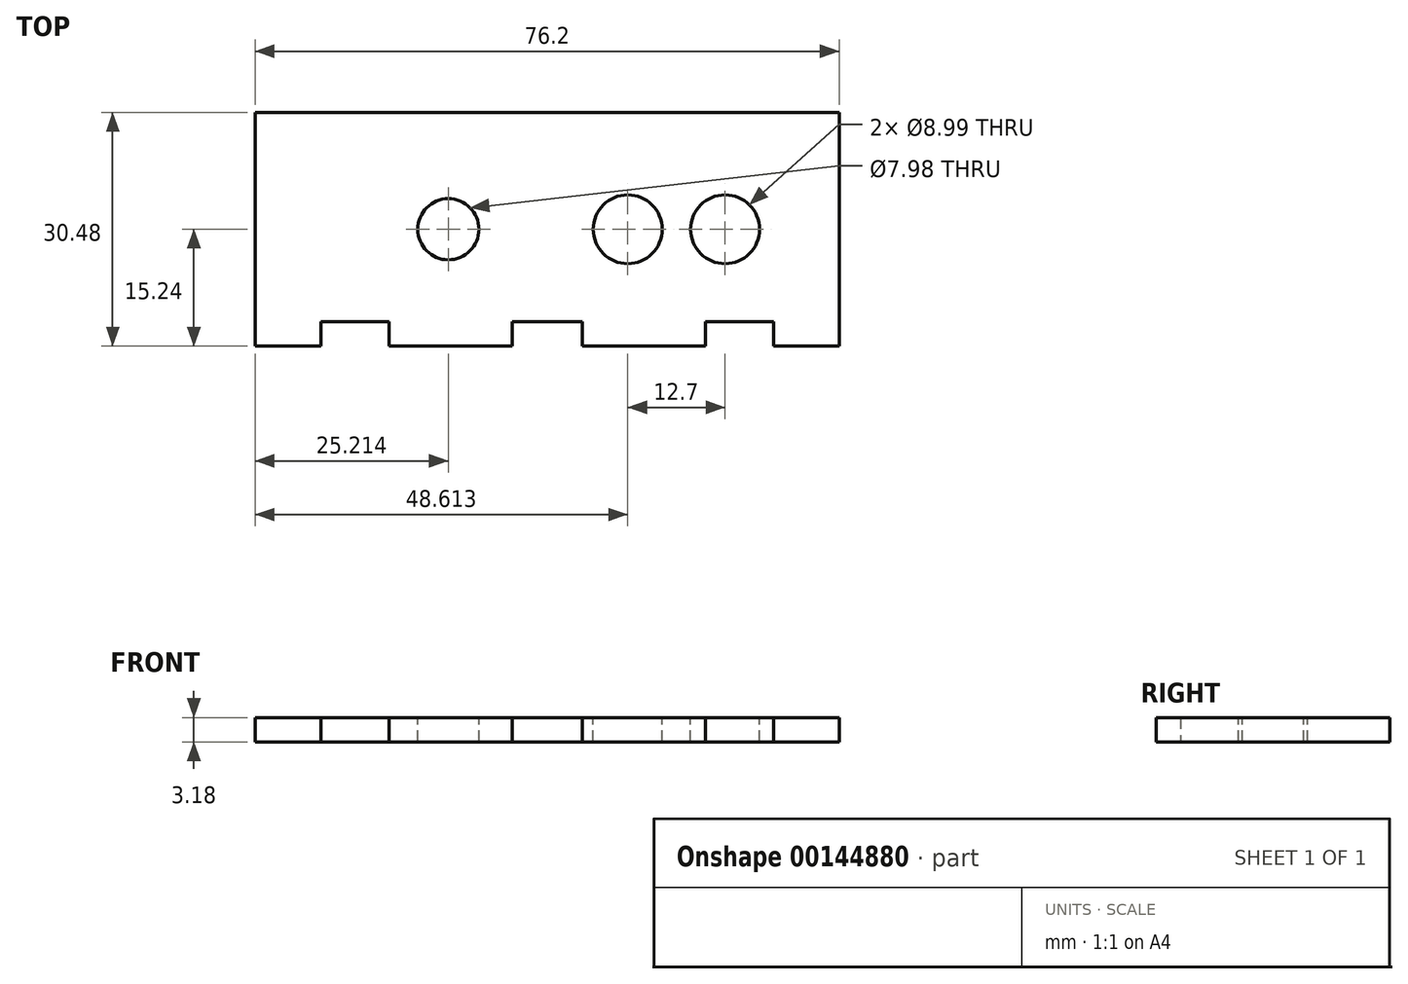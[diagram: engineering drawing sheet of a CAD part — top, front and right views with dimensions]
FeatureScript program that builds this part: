
annotation { "Feature Type Name" : "Feature", "Feature Type Description" : "" }
export const myFeature = defineFeature(function(context is Context, id is Id, definition is map)
    precondition{}
    {
        {
            var Q0;
            Q0=qCreatedBy(makeId("Top.planeOp"),FACE);
            var sketch = newSketch(context, id + "F0", { "sketchPlane" : qUnion([Q0])});
            skLineSegment(sketch, "E0.bottom", {"start": v(-38.1, 15.24) * mm, "end": v(38.1, 15.24) * mm});
            skLineSegment(sketch, "E0.top", {"start": v(-38.1, -15.24) * mm, "end": v(38.1, -15.24) * mm});
            skLineSegment(sketch, "E0.left", {"start": v(-38.1, 15.24) * mm, "end": v(-38.1, -15.24) * mm});
            skLineSegment(sketch, "E0.right", {"start": v(38.1, 15.24) * mm, "end": v(38.1, -15.24) * mm});
            skPoint(sketch, "E0.middle", {"position": v(0, 0) * mm});
            skLineSegment(sketch, "E1.bottom", {"start": v(-29.51, 15.24) * mm, "end": v(-20.62, 15.24) * mm});
            skLineSegment(sketch, "E2.bottom", {"start": v(29.51, 15.24) * mm, "end": v(20.62, 15.24) * mm});
            skLineSegment(sketch, "E3.top", {"start": v(-29.51, 18.42) * mm, "end": v(-20.62, 18.42) * mm});
            skLineSegment(sketch, "E3.left", {"start": v(-29.51, 15.24) * mm, "end": v(-29.51, 18.42) * mm});
            skLineSegment(sketch, "E3.right", {"start": v(-20.62, 15.24) * mm, "end": v(-20.62, 18.41) * mm});
            skLineSegment(sketch, "E4.top", {"start": v(20.62, 18.42) * mm, "end": v(29.51, 18.42) * mm});
            skLineSegment(sketch, "E4.left", {"start": v(20.62, 15.24) * mm, "end": v(20.62, 18.42) * mm});
            skLineSegment(sketch, "E4.right", {"start": v(29.51, 15.24) * mm, "end": v(29.51, 18.42) * mm});
            skPoint(sketch, "E5", {"position": v(0, 15.24) * mm});
            skPoint(sketch, "E6", {"position": v(-4.57, 15.24) * mm});
            skPoint(sketch, "E7", {"position": v(4.57, 15.24) * mm});
            skLineSegment(sketch, "E8.bottom", {"start": v(-4.57, 15.24) * mm, "end": v(4.57, 15.24) * mm});
            skLineSegment(sketch, "E8.top", {"start": v(-4.57, 18.42) * mm, "end": v(4.57, 18.42) * mm});
            skLineSegment(sketch, "E8.left", {"start": v(-4.57, 15.24) * mm, "end": v(-4.57, 18.42) * mm});
            skLineSegment(sketch, "E8.right", {"start": v(4.57, 15.24) * mm, "end": v(4.57, 18.42) * mm});
            skLineSegment(sketch, "E9.bottom", {"start": v(-29.51, -15.24) * mm, "end": v(-20.62, -15.24) * mm});
            skLineSegment(sketch, "E9.top", {"start": v(-29.51, -12.06) * mm, "end": v(-20.62, -12.06) * mm});
            skLineSegment(sketch, "E9.left", {"start": v(-29.51, -15.24) * mm, "end": v(-29.51, -12.06) * mm});
            skLineSegment(sketch, "E9.right", {"start": v(-20.62, -15.24) * mm, "end": v(-20.62, -12.06) * mm});
            skLineSegment(sketch, "E10.bottom", {"start": v(-4.57, -15.24) * mm, "end": v(4.57, -15.24) * mm});
            skLineSegment(sketch, "E10.top", {"start": v(-4.57, -12.06) * mm, "end": v(4.57, -12.06) * mm});
            skLineSegment(sketch, "E10.left", {"start": v(-4.57, -15.24) * mm, "end": v(-4.57, -12.06) * mm});
            skLineSegment(sketch, "E10.right", {"start": v(4.57, -15.24) * mm, "end": v(4.57, -12.06) * mm});
            skLineSegment(sketch, "E11.bottom", {"start": v(20.62, -15.24) * mm, "end": v(29.51, -15.24) * mm});
            skLineSegment(sketch, "E11.top", {"start": v(20.62, -12.06) * mm, "end": v(29.51, -12.06) * mm});
            skLineSegment(sketch, "E11.left", {"start": v(20.62, -15.24) * mm, "end": v(20.62, -12.06) * mm});
            skLineSegment(sketch, "E11.right", {"start": v(29.51, -15.24) * mm, "end": v(29.51, -12.06) * mm});
            skSolve(sketch);
        }
        {
            var Q0;
            Q0=makeQuery(id+"F0.imprint","IMPRINT",FACE,{"disambiguationData":[TD([[makeQuery(id+"F0.imprint","IMPRINT",EDGE,{"derivedFrom":sQuery(id+"F0.wireOp",EDGE,"E1.bottom")}),1.0]])]});
            var Q1;
            Q1=makeQuery(id+"F0.imprint","IMPRINT",FACE,{"disambiguationData":[TD([[makeQuery(id+"F0.imprint","IMPRINT",EDGE,{"derivedFrom":sQuery(id+"F0.wireOp",EDGE,"E0.top")}),1.0]])]});
            var Q2;
            Q2=makeQuery(id+"F0.imprint","IMPRINT",FACE,{"disambiguationData":[TD([[makeQuery(id+"F0.imprint","IMPRINT",EDGE,{"derivedFrom":sQuery(id+"F0.wireOp",EDGE,"E8.bottom")}),1.0]])]});
            var Q3;
            Q3=makeQuery(id+"F0.imprint","IMPRINT",FACE,{"disambiguationData":[TD([[makeQuery(id+"F0.imprint","IMPRINT",EDGE,{"derivedFrom":sQuery(id+"F0.wireOp",EDGE,"E2.bottom")}),-1.0]])]});
            extrude(context, id + "F1", {"entities" : qUnion([Q0, Q1, Q2, Q3]), "depth" : 3.17 * mm});
        }
        {
            var Q0;
            Q0=makeQuery(id+"F1.opExtrude","CAP_FACE",FACE,{"disambiguationData":[OSD([sQuery(id+"F0.wireOp",EDGE,"E0.bottom"),sQuery(id+"F0.wireOp",EDGE,"E0.top"),sQuery(id+"F0.wireOp",EDGE,"E0.left"),sQuery(id+"F0.wireOp",EDGE,"E0.right"),sQuery(id+"F0.wireOp",EDGE,"E3.top"),sQuery(id+"F0.wireOp",EDGE,"E3.left"),sQuery(id+"F0.wireOp",EDGE,"E3.right"),sQuery(id+"F0.wireOp",EDGE,"E4.top"),sQuery(id+"F0.wireOp",EDGE,"E4.left"),sQuery(id+"F0.wireOp",EDGE,"E4.right"),sQuery(id+"F0.wireOp",EDGE,"E8.top"),sQuery(id+"F0.wireOp",EDGE,"E8.left"),sQuery(id+"F0.wireOp",EDGE,"E8.right"),sQuery(id+"F0.wireOp",EDGE,"E9.top"),sQuery(id+"F0.wireOp",EDGE,"E9.left"),sQuery(id+"F0.wireOp",EDGE,"E9.right"),sQuery(id+"F0.wireOp",EDGE,"E10.top"),sQuery(id+"F0.wireOp",EDGE,"E10.left"),sQuery(id+"F0.wireOp",EDGE,"E10.right"),sQuery(id+"F0.wireOp",EDGE,"E11.top"),sQuery(id+"F0.wireOp",EDGE,"E11.left"),sQuery(id+"F0.wireOp",EDGE,"E11.right")])],"isStart":false});
            var sketch = newSketch(context, id + "F2", { "sketchPlane" : qUnion([Q0])});
            skCircle(sketch, "E12", {"center": v(-12.89, 0) * mm, "radius": 3.99 * mm});
            skCircle(sketch, "E13", {"center": v(10.51, 0) * mm, "radius": 4.5 * mm});
            skCircle(sketch, "E14", {"center": v(23.21, 0) * mm, "radius": 4.5 * mm});
            skSolve(sketch);
        }
        {
            var Q0;
            Q0=makeQuery(id+"F2.imprint","IMPRINT",FACE,{"disambiguationData":[TD([[makeQuery(id+"F2.imprint","IMPRINT",EDGE,{"derivedFrom":sQuery(id+"F2.wireOp",EDGE,"E12")}),1.0]])]});
            var Q1;
            Q1=makeQuery(id+"F2.imprint","IMPRINT",FACE,{"disambiguationData":[TD([[makeQuery(id+"F2.imprint","IMPRINT",EDGE,{"derivedFrom":sQuery(id+"F2.wireOp",EDGE,"E13")}),1.0]])]});
            var Q2;
            Q2=makeQuery(id+"F2.imprint","IMPRINT",FACE,{"disambiguationData":[TD([[makeQuery(id+"F2.imprint","IMPRINT",EDGE,{"derivedFrom":sQuery(id+"F2.wireOp",EDGE,"E14")}),1.0]])]});
            extrude(context, id + "F3", {"entities" : qUnion([Q0, Q1, Q2]), "operationType" : NewBodyOperationType.REMOVE, "oppositeDirection" : true, "depth" : 25.4 * mm});
        }
    });
